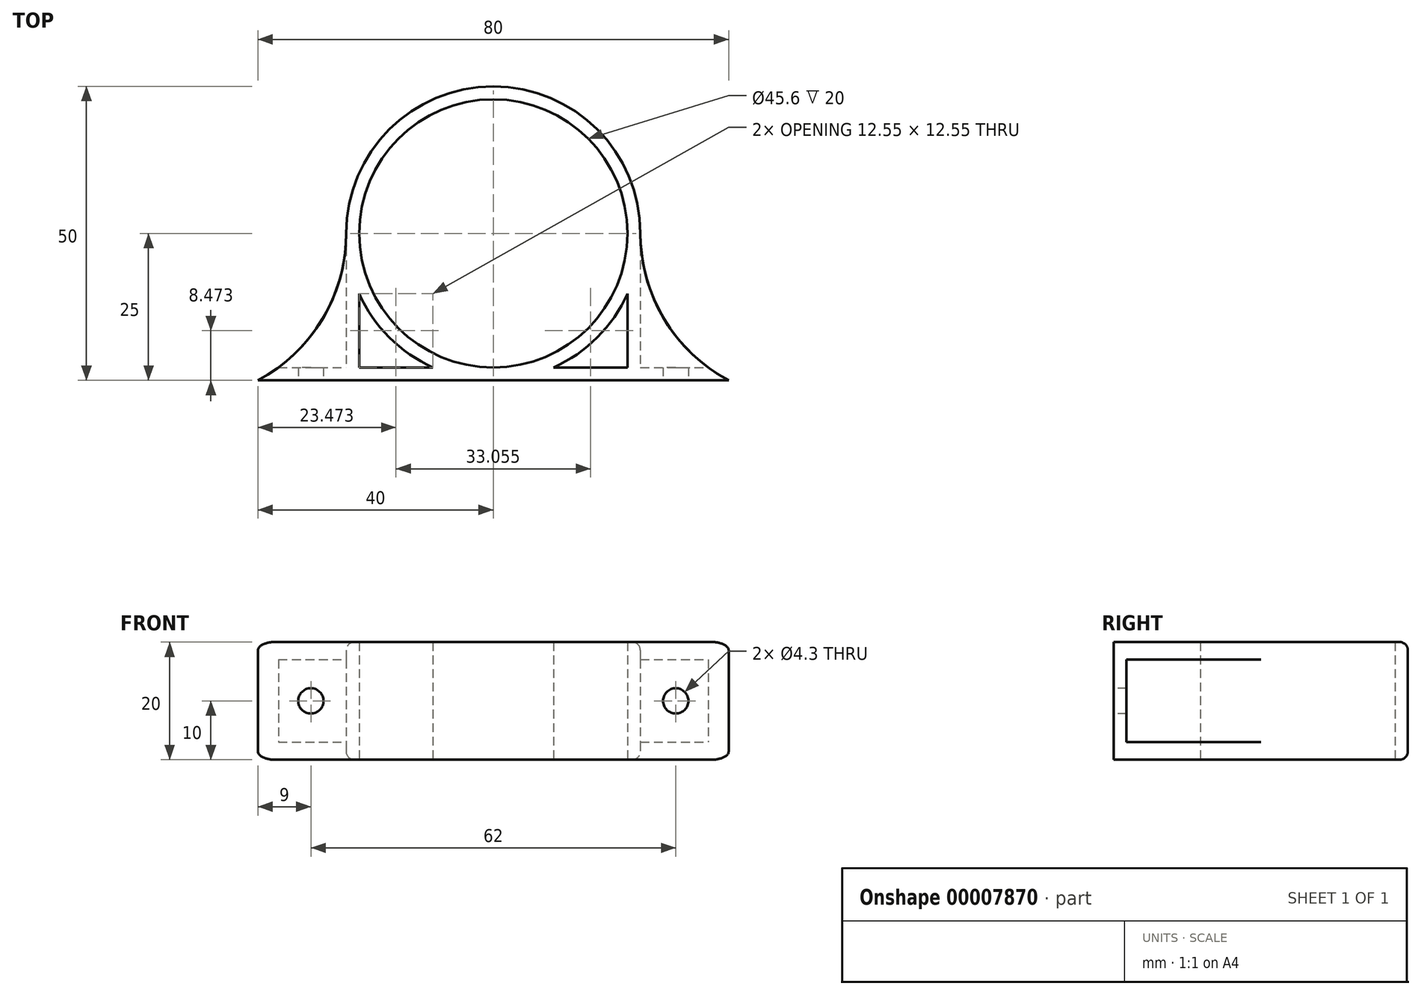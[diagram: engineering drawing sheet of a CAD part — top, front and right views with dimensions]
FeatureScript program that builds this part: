
annotation { "Feature Type Name" : "Feature", "Feature Type Description" : "" }
export const myFeature = defineFeature(function(context is Context, id is Id, definition is map)
    precondition{}
    {
        {
            var Q0;
            Q0=qCreatedBy(makeId("Top.planeOp"),FACE);
            var sketch = newSketch(context, id + "F0", { "sketchPlane" : qUnion([Q0])});
            skCircle(sketch, "E0", {"center": v(40, 25) * mm, "radius": 22.8 * mm});
            skArc(sketch, "E1", {"start": v(50.25, 2.2) * mm, "mid": v(57.68, 7.32) * mm, "end": v(62.8, 14.75) * mm});
            skLineSegment(sketch, "E2", {"start": v(0, 0) * mm, "end": v(80, 0) * mm});
            skPoint(sketch, "E3", {"position": v(40, 0) * mm});
            skArc(sketch, "E4", {"start": v(0, 0) * mm, "mid": v(10.96, 10.42) * mm, "end": v(15, 25) * mm});
            skArc(sketch, "E5", {"start": v(65, 25) * mm, "mid": v(69.04, 10.42) * mm, "end": v(80, 0) * mm});
            skLineSegment(sketch, "E6", {"start": v(3.49, 2.2) * mm, "end": v(15, 2.2) * mm});
            skLineSegment(sketch, "E7.trimOffspring", {"start": v(50.25, 2.2) * mm, "end": v(62.8, 2.2) * mm});
            skLineSegment(sketch, "E8", {"start": v(15, 25) * mm, "end": v(15, 2.2) * mm});
            skLineSegment(sketch, "E9", {"start": v(65, 25) * mm, "end": v(65, 2.2) * mm});
            skLineSegment(sketch, "E10", {"start": v(17.2, 2.2) * mm, "end": v(17.2, 14.75) * mm});
            skLineSegment(sketch, "E11", {"start": v(62.8, 2.2) * mm, "end": v(62.8, 14.75) * mm});
            skArc(sketch, "E12.trimOffspring", {"start": v(17.2, 14.75) * mm, "mid": v(22.32, 7.32) * mm, "end": v(29.75, 2.2) * mm});
            skLineSegment(sketch, "E13.trimOffspring", {"start": v(17.2, 2.2) * mm, "end": v(29.75, 2.2) * mm});
            skArc(sketch, "E14.trimOffspring", {"start": v(65, 25) * mm, "mid": v(40, 50) * mm, "end": v(15, 25) * mm});
            skLineSegment(sketch, "E15.trimOffspring", {"start": v(65, 2.2) * mm, "end": v(76.51, 2.2) * mm});
            skSolve(sketch);
        }
        {
            var Q0;
            Q0=makeQuery(id+"F0.imprint","IMPRINT",FACE,{"disambiguationData":[TD([[makeQuery(id+"F0.imprint","IMPRINT",EDGE,{"derivedFrom":sQuery(id+"F0.wireOp",EDGE,"E0")}),-1.0]])]});
            var Q1;
            {var subQ1=sQuery(id+"F0.wireOp",EDGE,"E6");Q1=makeQuery(id+"F0.imprint","IMPRINT",FACE,{"disambiguationData":[TD([[makeQuery(id+"F0.imprint","IMPRINT",EDGE,{"derivedFrom":subQ1}),1.0]])]});}
            var Q2;
            {var subQ1=sQuery(id+"F0.wireOp",EDGE,"E9");Q2=makeQuery(id+"F0.imprint","IMPRINT",FACE,{"disambiguationData":[TD([[makeQuery(id+"F0.imprint","IMPRINT",EDGE,{"derivedFrom":subQ1}),1.0]])]});}
            extrude(context, id + "F1", {"entities" : qUnion([Q0, Q1, Q2]), "endBound" : BoundingType.SYMMETRIC, "depth" : 20 * mm});
        }
        {
            var Q0;
            {var subQ1=sQuery(id+"F0.wireOp",EDGE,"E9");Q0=makeQuery(id+"F0.imprint","IMPRINT",FACE,{"disambiguationData":[TD([[makeQuery(id+"F0.imprint","IMPRINT",EDGE,{"derivedFrom":subQ1}),1.0]])]});}
            var Q1;
            {var subQ1=sQuery(id+"F0.wireOp",EDGE,"E6");Q1=makeQuery(id+"F0.imprint","IMPRINT",FACE,{"disambiguationData":[TD([[makeQuery(id+"F0.imprint","IMPRINT",EDGE,{"derivedFrom":subQ1}),1.0]])]});}
            extrude(context, id + "F2", {"entities" : qUnion([Q0, Q1]), "operationType" : NewBodyOperationType.REMOVE, "endBound" : BoundingType.SYMMETRIC, "depth" : 14 * mm});
        }
        {
            var Q0;
            Q0=makeQuery(id+"F1.opExtrude","SWEPT_FACE",FACE,{"disambiguationData":[OSD([sQuery(id+"F0.wireOp",EDGE,"E2")])]});
            var sketch = newSketch(context, id + "F3", { "sketchPlane" : qUnion([Q0])});
            skCircle(sketch, "E16", {"center": v(71, 0) * mm, "radius": 2.15 * mm});
            skCircle(sketch, "E17", {"center": v(9, 0) * mm, "radius": 2.15 * mm});
            skSolve(sketch);
        }
        {
            var Q0;
            Q0 = qSketchRegion(id + "F3", true);
            extrude(context, id + "F4", {"entities" : qUnion([Q0]), "operationType" : NewBodyOperationType.REMOVE, "endBound" : BoundingType.THROUGH_ALL, "oppositeDirection" : true, "depth" : 25 * mm});
        }
        {
            var Q0;
            Q0=makeQuery(id+"F1.opExtrude","CAP_EDGE",EDGE,{"disambiguationData":[OSD([sQuery(id+"F0.wireOp",EDGE,"E14.trimOffspring")])],"isStart":false});
            var Q1;
            Q1=makeQuery(id+"F1.opExtrude","CAP_EDGE",EDGE,{"disambiguationData":[OSD([sQuery(id+"F0.wireOp",EDGE,"E14.trimOffspring")])],"isStart":true});
            var Q2;
            Q2=makeQuery(id+"F1.opExtrude","CAP_EDGE",EDGE,{"disambiguationData":[OSD([sQuery(id+"F0.wireOp",EDGE,"E5")])],"isStart":true});
            var Q3;
            Q3=makeQuery(id+"F1.opExtrude","CAP_EDGE",EDGE,{"disambiguationData":[OSD([sQuery(id+"F0.wireOp",EDGE,"E5")])],"isStart":false});
            var Q4;
            Q4=makeQuery(id+"F1.opExtrude","CAP_EDGE",EDGE,{"disambiguationData":[OSD([sQuery(id+"F0.wireOp",EDGE,"E4")])],"isStart":true});
            fillet(context, id + "F5", {"entities" : qUnion([Q0, Q1, Q2, Q3, Q4]), "radius" : 1.4 * mm, "tangentPropagation" : true, "allowEdgeOverflow" : false});
        }
    });
